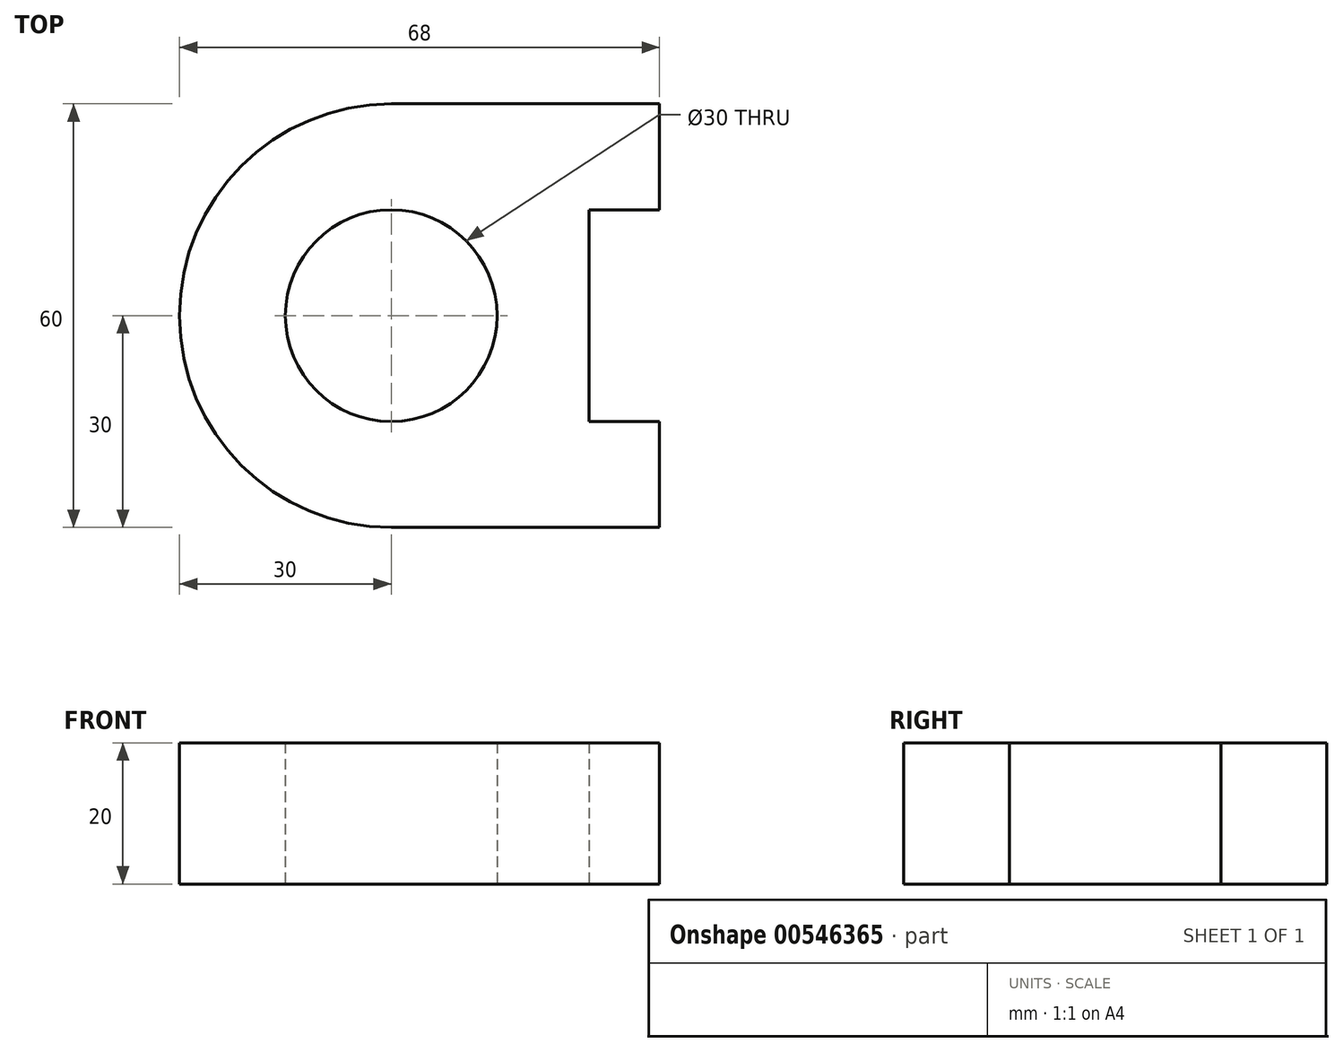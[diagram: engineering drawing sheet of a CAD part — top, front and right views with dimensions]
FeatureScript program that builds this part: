
annotation { "Feature Type Name" : "Feature", "Feature Type Description" : "" }
export const myFeature = defineFeature(function(context is Context, id is Id, definition is map)
    precondition{}
    {
        {
            var Q0;
            Q0=qCreatedBy(makeId("Top.planeOp"),FACE);
            var sketch = newSketch(context, id + "F0", { "sketchPlane" : qUnion([Q0])});
            skLineSegment(sketch, "E0", {"start": v(-254.18, 30) * mm, "end": v(206.58, 30) * mm, "construction": true});
            skLineSegment(sketch, "E1", {"start": v(-254.18, -30) * mm, "end": v(206.58, -30) * mm, "construction": true});
            skArc(sketch, "E2", {"start": v(0, 30) * mm, "mid": v(-30, 0) * mm, "end": v(0, -30) * mm});
            skLineSegment(sketch, "E3", {"start": v(0, 30) * mm, "end": v(38, 30) * mm});
            skLineSegment(sketch, "E4", {"start": v(38, 30) * mm, "end": v(38, 15) * mm});
            skLineSegment(sketch, "E5", {"start": v(38, 15) * mm, "end": v(28, 15) * mm});
            skLineSegment(sketch, "E6", {"start": v(28, 15) * mm, "end": v(28, -15) * mm});
            skLineSegment(sketch, "E7", {"start": v(28, -15) * mm, "end": v(38, -15) * mm});
            skLineSegment(sketch, "E8", {"start": v(38, -15) * mm, "end": v(38, -30) * mm});
            skLineSegment(sketch, "E9", {"start": v(38, -30) * mm, "end": v(0, -30) * mm});
            skCircle(sketch, "E10", {"center": v(0, 0) * mm, "radius": 15 * mm});
            skSolve(sketch);
        }
        {
            var Q0;
            Q0 = qSketchRegion(id + "F0", true);
            extrude(context, id + "F1", {"entities" : qUnion([Q0]), "depth" : 20 * mm, "offsetDistance" : 25 * mm});
        }
    });
